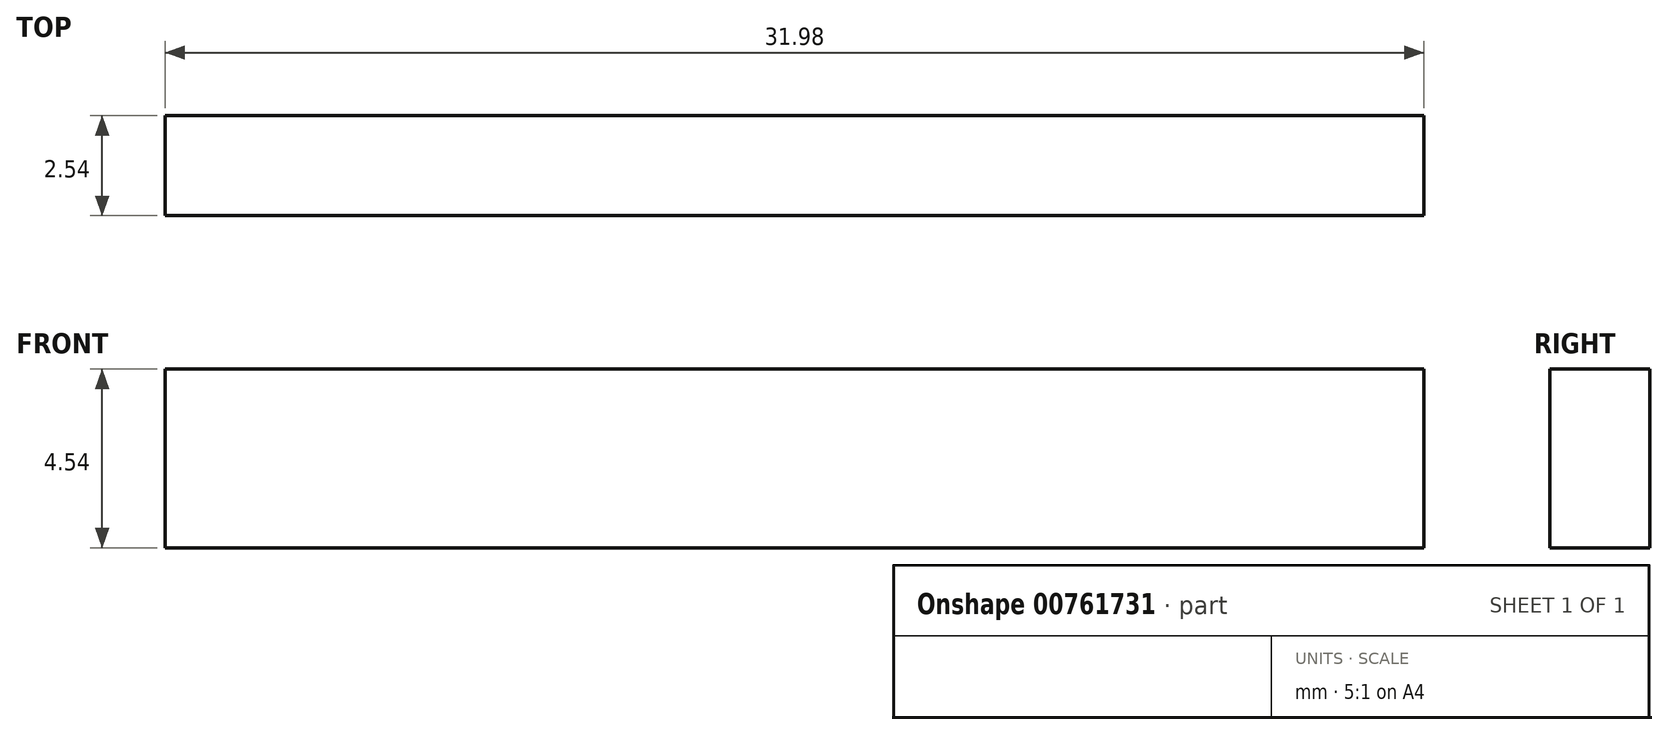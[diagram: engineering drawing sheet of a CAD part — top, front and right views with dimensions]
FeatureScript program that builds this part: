
annotation { "Feature Type Name" : "Feature", "Feature Type Description" : "" }
export const myFeature = defineFeature(function(context is Context, id is Id, definition is map)
    precondition{}
    {
        {
            var Q0;
            Q0=qCreatedBy(makeId("Front.planeOp"),FACE);
            var sketch = newSketch(context, id + "F0", { "sketchPlane" : qUnion([Q0])});
            skLineSegment(sketch, "E0.bottom", {"start": v(-13.62, 4.54) * mm, "end": v(18.36, 4.54) * mm});
            skLineSegment(sketch, "E0.top", {"start": v(-13.62, 0) * mm, "end": v(18.36, 0) * mm});
            skLineSegment(sketch, "E0.left", {"start": v(-13.62, 4.54) * mm, "end": v(-13.62, 0) * mm});
            skLineSegment(sketch, "E0.right", {"start": v(18.36, 4.54) * mm, "end": v(18.36, 0) * mm});
            skSolve(sketch);
        }
        {
            var Q0;
            Q0=makeQuery(id+"F0.imprint","IMPRINT",FACE,{"disambiguationData":[TD([[makeQuery(id+"F0.imprint","IMPRINT",EDGE,{"derivedFrom":sQuery(id+"F0.wireOp",EDGE,"E0.bottom")}),-1.0]])]});
            extrude(context, id + "F1", {"entities" : qUnion([Q0]), "depth" : 2.54 * mm, "offsetDistance" : 25.4 * mm});
        }
    });
